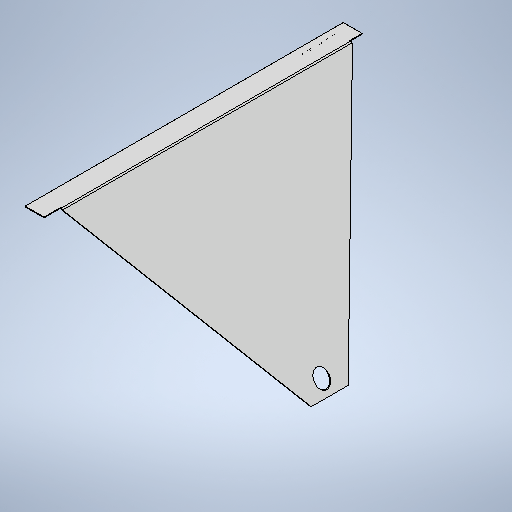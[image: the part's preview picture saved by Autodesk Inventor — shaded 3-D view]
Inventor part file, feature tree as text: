
AUTODESK INVENTOR PART (.ipt)
format: ipt  version: 2025 (Build 290162010, 162A)  size: 442,368 bytes
history: native  units: mm
features: sketch x5, other x4, sheet_metal_op x3, extrude x3, projected_geometry x1
ambient origin geometry x8: Origin, YZ Plane, XZ Plane, XY Plane, X Axis, Y Axis, Z Axis, Center Point
bodies: Body1 (feature_tree)
feature tree (16):
  sheet_metal_op  "Contour Flange2"
  extrude  "Extrusion7"  Depth=88.0mm
  extrude  "Extrusion11"  Depth=230.0mm
  extrude  "Extrusion14"  Depth=4.0mm
  other  "Mark2"
  other  "A-Side Definition"
  sketch  "Sketch1"  dims[d0=1150.0mm d61=88.0mm]
  other  "Plate4"
  sheet_metal_op  "Bend4"
  sheet_metal_op  "Corner4"
  sketch  "Sketch10"  dims[d63=10.0mm d64=230.0mm]
  sketch  "Sketch14"  dims[d65=800.0mm d66=4.0mm]
  sketch  "Sketch17"  dims[d67=4.0mm]
  projected_geometry  "Projected Loop11"
  sketch  "Sketch19"  dims[d68=2.0mm d69=8.0mm d70=6.0mm d71=1536.0mm d72=6.0mm d73=4.0mm d74=16.0mm d75=4.0mm d76=6.0mm d81=10.0mm d82=0.0mm d86=60.0mm d99=76.5mm d100=0.0mm d101=0.0mm d102=60.0mm d103=50.0mm d110=3.0mm d111=196.0mm d112=66.0mm d113=100.0mm d114=87.0mm d115=100.0mm d116=4.0mm d117=0.0mm]
  other  "Definition1"
